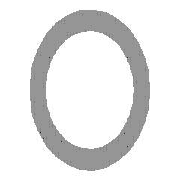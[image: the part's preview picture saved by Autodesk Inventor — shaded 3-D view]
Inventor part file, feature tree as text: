
AUTODESK INVENTOR PART (.ipt)
format: ipt  version: 2017 (Build 210142000, 142)  size: 117,760 bytes
history: native  units: mm (DEFAULTED — no unit token found)
features: other x3, sketch x3, plane x1
ambient origin geometry x8: Origin, YZ Plane, XZ Plane, XY Plane, X Axis, Y Axis, Z Axis, Center Point
bodies: Solid1 (feature_tree), Body (feature_tree)
feature tree (7):
  other  "Driven Length"
  other  "Start plane"
  other  "End plane"
  sketch  "Sketch"  dims[d2=258.5mm d3=0.0mm d4=-0.0mm d5=258.5mm d6=90.0deg d7=258.5mm]
  sketch  "Sketch3"  dims[d0=25.0mm]
  plane  "Work Plane3"
  sketch  "Sketch4"  dims[d1=1.5mm]
